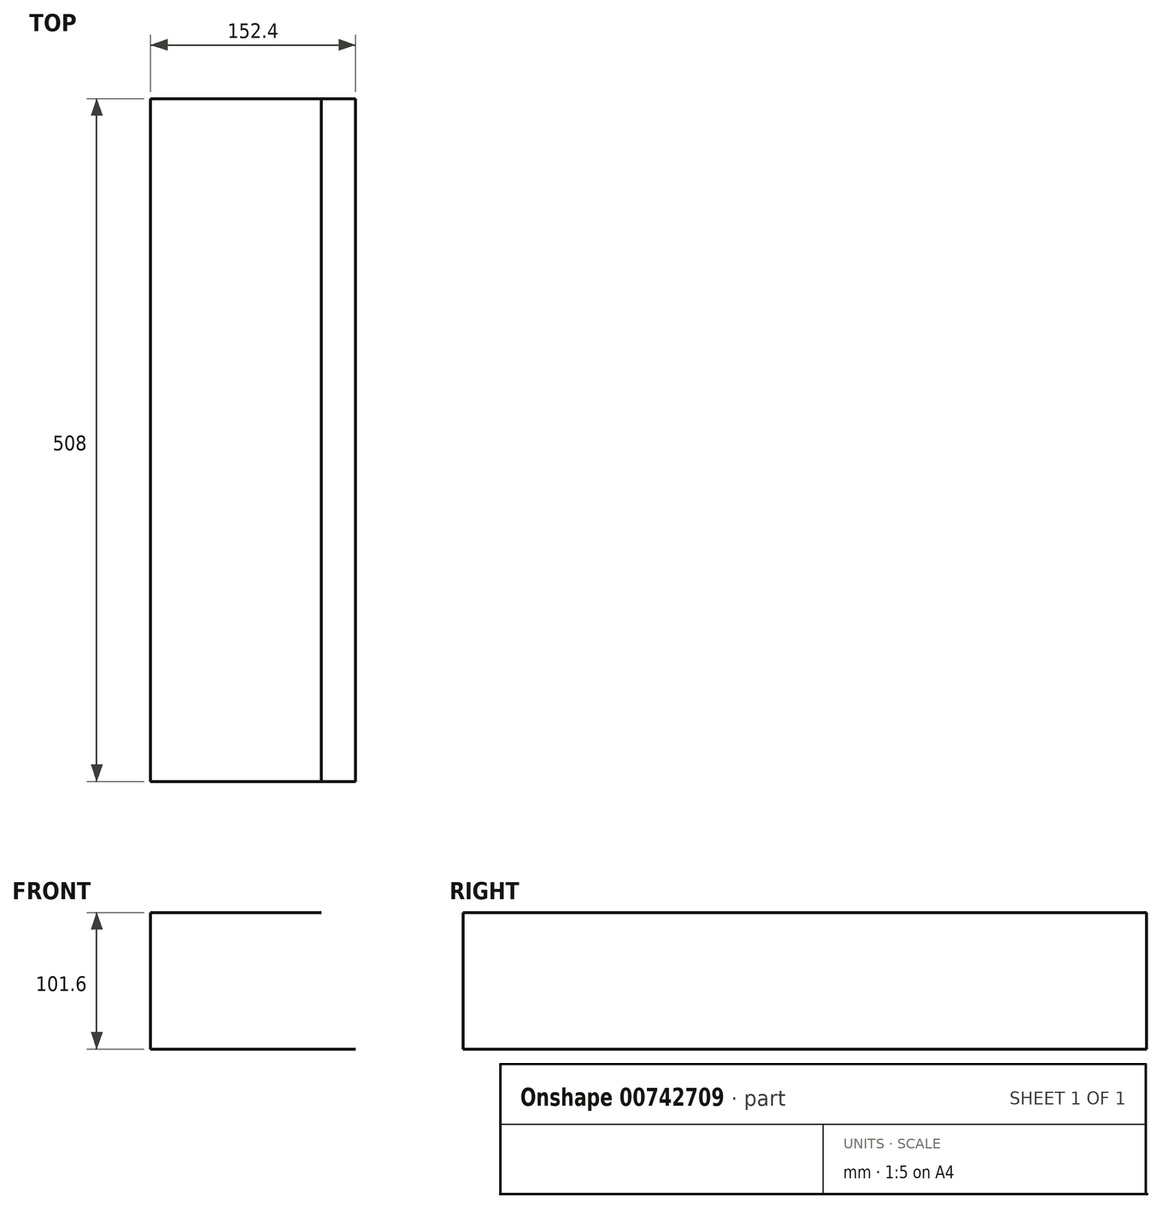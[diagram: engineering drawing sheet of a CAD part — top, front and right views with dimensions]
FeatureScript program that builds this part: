
annotation { "Feature Type Name" : "Feature", "Feature Type Description" : "" }
export const myFeature = defineFeature(function(context is Context, id is Id, definition is map)
    precondition{}
    {
        {
            var Q0;
            Q0=qCreatedBy(makeId("Front.planeOp"),FACE);
            var sketch = newSketch(context, id + "F0", { "sketchPlane" : qUnion([Q0])});
            skLineSegment(sketch, "E0", {"start": v(-60.4, 0) * mm, "end": v(-212.8, 0) * mm});
            skLineSegment(sketch, "E1", {"start": v(-212.8, 0) * mm, "end": v(-212.8, 101.6) * mm});
            skLineSegment(sketch, "E2", {"start": v(-212.8, 101.6) * mm, "end": v(-85.8, 101.6) * mm});
            skSolve(sketch);
        }
        {
            var Q0;
            Q0 = qSketchRegion(id + "F0", true);
            var Q1;
            Q1=sQuery(id+"F0.wireOp",EDGE,"E2");
            var Q2;
            Q2=sQuery(id+"F0.wireOp",EDGE,"E1");
            var Q3;
            Q3=sQuery(id+"F0.wireOp",EDGE,"E0");
            extrude(context, id + "F1", {"entities" : qUnion([Q0]), "bodyType" : ToolBodyType.SURFACE, "surfaceEntities" : qUnion([Q1, Q2, Q3]), "depth" : 508 * mm, "offsetDistance" : 25.4 * mm});
        }
    });
